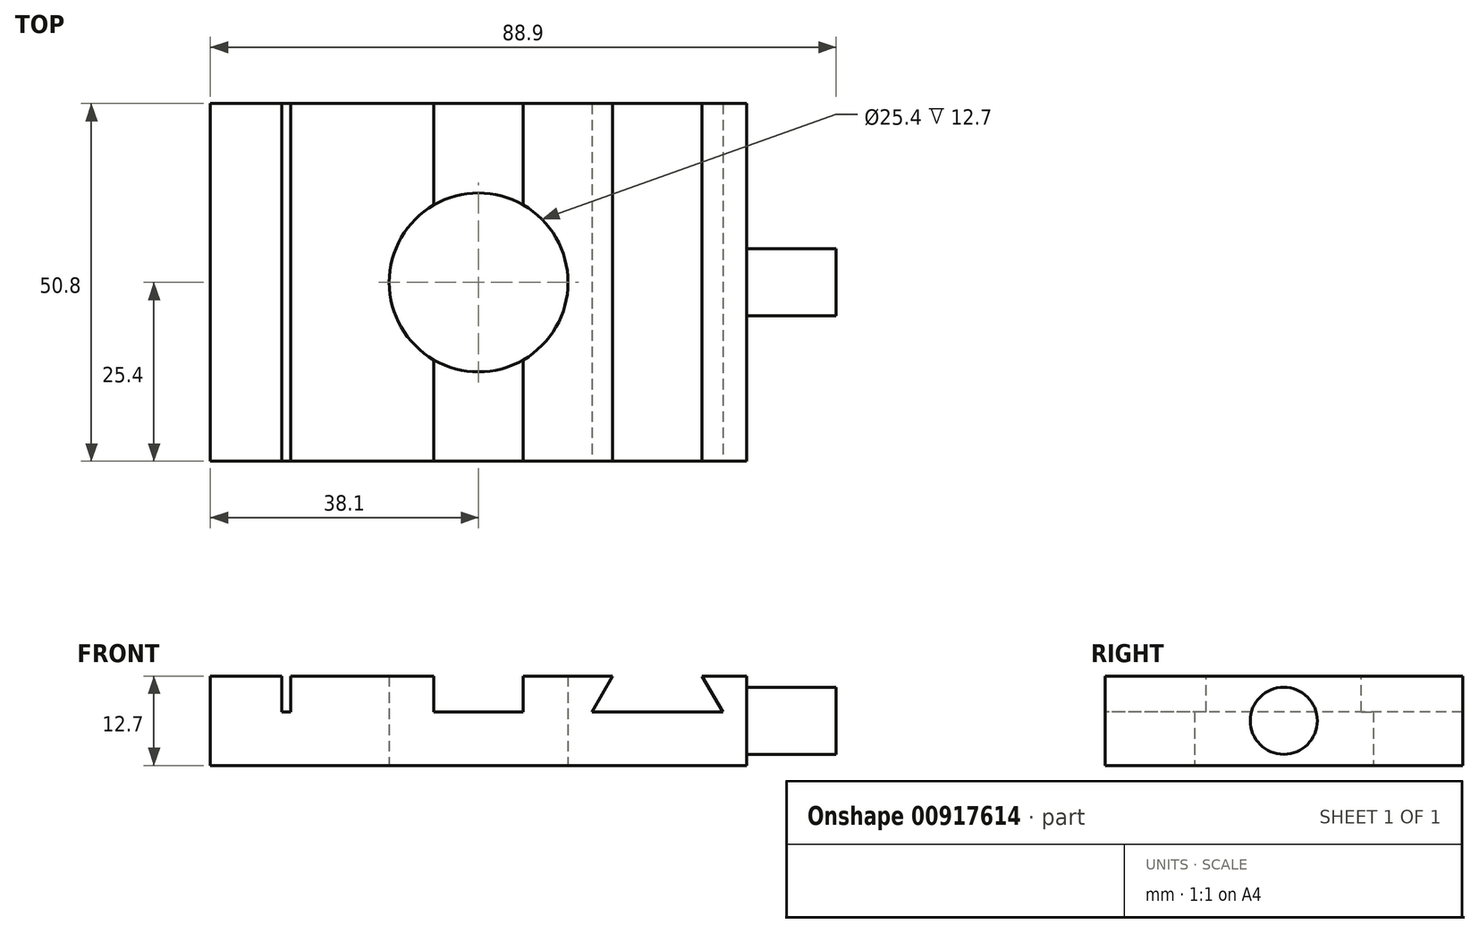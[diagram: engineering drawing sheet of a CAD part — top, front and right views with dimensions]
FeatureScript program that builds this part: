
annotation { "Feature Type Name" : "Feature", "Feature Type Description" : "" }
export const myFeature = defineFeature(function(context is Context, id is Id, definition is map)
    precondition{}
    {
        {
            var Q0;
            Q0=qCreatedBy(makeId("Top.planeOp"),FACE);
            var sketch = newSketch(context, id + "F0", { "sketchPlane" : qUnion([Q0])});
            skLineSegment(sketch, "E0.bottom", {"start": v(-38.1, 25.4) * mm, "end": v(38.1, 25.4) * mm});
            skLineSegment(sketch, "E0.top", {"start": v(-38.1, -25.4) * mm, "end": v(38.1, -25.4) * mm});
            skLineSegment(sketch, "E0.left", {"start": v(-38.1, 25.4) * mm, "end": v(-38.1, -25.4) * mm});
            skLineSegment(sketch, "E0.right", {"start": v(38.1, 25.4) * mm, "end": v(38.1, -25.4) * mm});
            skPoint(sketch, "E0.middle", {"position": v(0, 0) * mm});
            skCircle(sketch, "E1", {"center": v(0, 0) * mm, "radius": 12.7 * mm});
            skSolve(sketch);
        }
        {
            var Q0;
            Q0=makeQuery(id+"F0.imprint","IMPRINT",FACE,{"disambiguationData":[TD([[makeQuery(id+"F0.imprint","IMPRINT",EDGE,{"derivedFrom":sQuery(id+"F0.wireOp",EDGE,"E0.bottom")}),-1.0]])]});
            extrude(context, id + "F1", {"entities" : qUnion([Q0]), "flatOperationType" : FlatOperationType.REMOVE, "depth" : 12.7 * mm, "offsetDistance" : 25.4 * mm, "domain" : OperationDomain.MODEL});
        }
        {
            var Q0;
            Q0=makeQuery(id+"F1.opExtrude","CAP_FACE",FACE,{"disambiguationData":[OSD([sQuery(id+"F0.wireOp",EDGE,"E0.bottom"),sQuery(id+"F0.wireOp",EDGE,"E0.top"),sQuery(id+"F0.wireOp",EDGE,"E0.left"),sQuery(id+"F0.wireOp",EDGE,"E0.right"),sQuery(id+"F0.wireOp",EDGE,"E1")])],"isStart":false});
            var sketch = newSketch(context, id + "F2", { "sketchPlane" : qUnion([Q0])});
            skLineSegment(sketch, "E2.bottom", {"start": v(-27.94, 25.4) * mm, "end": v(-26.67, 25.4) * mm});
            skLineSegment(sketch, "E2.top", {"start": v(-27.94, -25.4) * mm, "end": v(-26.67, -25.4) * mm});
            skLineSegment(sketch, "E2.left", {"start": v(-27.94, 25.4) * mm, "end": v(-27.94, -25.4) * mm});
            skLineSegment(sketch, "E2.right", {"start": v(-26.67, 25.4) * mm, "end": v(-26.67, -25.4) * mm});
            skPoint(sketch, "E3", {"position": v(0, 0) * mm});
            skLineSegment(sketch, "E4.bottom", {"start": v(-6.35, 25.4) * mm, "end": v(6.35, 25.4) * mm});
            skLineSegment(sketch, "E4.top", {"start": v(-6.35, -25.4) * mm, "end": v(6.35, -25.4) * mm});
            skLineSegment(sketch, "E4.left", {"start": v(-6.35, 25.4) * mm, "end": v(-6.35, -25.4) * mm});
            skLineSegment(sketch, "E4.right", {"start": v(6.35, 25.4) * mm, "end": v(6.35, -25.4) * mm});
            skLineSegment(sketch, "E5", {"start": v(0, 25.4) * mm, "end": v(0, -25.4) * mm, "construction": true});
            skSolve(sketch);
        }
        {
            var Q0;
            Q0=makeQuery(id+"F2.imprint","IMPRINT",FACE,{"disambiguationData":[TD([[makeQuery(id+"F2.imprint","IMPRINT",EDGE,{"derivedFrom":sQuery(id+"F2.wireOp",EDGE,"E2.bottom")}),-1.0]])]});
            var Q1;
            {var subQ0=sQuery(id+"F2.wireOp",EDGE,"E4.bottom");Q1=makeQuery(id+"F2.imprint","IMPRINT",FACE,{"disambiguationData":[TD([[makeQuery(id+"F2.imprint","IMPRINT",EDGE,{"derivedFrom":subQ0}),-1.0]])]});}
            var Q2;
            {var subQ0=sQuery(id+"F2.wireOp",EDGE,"E4.top");Q2=makeQuery(id+"F2.imprint","IMPRINT",FACE,{"disambiguationData":[TD([[makeQuery(id+"F2.imprint","IMPRINT",EDGE,{"derivedFrom":subQ0}),1.0]])]});}
            extrude(context, id + "F3", {"entities" : qUnion([Q0, Q1, Q2]), "operationType" : NewBodyOperationType.REMOVE, "oppositeDirection" : true, "depth" : 5.08 * mm, "offsetDistance" : 25.4 * mm});
        }
        {
            var Q0;
            Q0=makeQuery(id+"F1.opExtrude","SWEPT_FACE",FACE,{"disambiguationData":[OSD([sQuery(id+"F0.wireOp",EDGE,"E0.top")])]});
            var sketch = newSketch(context, id + "F4", { "sketchPlane" : qUnion([Q0])});
            skLineSegment(sketch, "E6", {"start": v(19.05, 12.7) * mm, "end": v(16.12, 7.62) * mm});
            skLineSegment(sketch, "E7", {"start": v(16.12, 7.62) * mm, "end": v(34.68, 7.62) * mm});
            skLineSegment(sketch, "E8", {"start": v(34.68, 7.62) * mm, "end": v(31.75, 12.7) * mm});
            skLineSegment(sketch, "E9", {"start": v(31.75, 12.7) * mm, "end": v(19.05, 12.7) * mm});
            skLineSegment(sketch, "E10", {"start": v(25.4, 7.62) * mm, "end": v(25.4, 12.7) * mm, "construction": true});
            skSolve(sketch);
        }
        {
            var Q0;
            Q0=makeQuery(id+"F4.imprint","IMPRINT",FACE,{"disambiguationData":[TD([[makeQuery(id+"F4.imprint","IMPRINT",EDGE,{"derivedFrom":sQuery(id+"F4.wireOp",EDGE,"E6")}),1.0]])]});
            extrude(context, id + "F5", {"entities" : qUnion([Q0]), "operationType" : NewBodyOperationType.REMOVE, "endBound" : BoundingType.THROUGH_ALL, "oppositeDirection" : true, "depth" : 25.4 * mm, "offsetDistance" : 25.4 * mm});
        }
        {
            var Q0;
            Q0=makeQuery(id+"F1.opExtrude","SWEPT_FACE",FACE,{"disambiguationData":[OSD([sQuery(id+"F0.wireOp",EDGE,"E0.right")])]});
            var sketch = newSketch(context, id + "F6", { "sketchPlane" : qUnion([Q0])});
            skCircle(sketch, "E11", {"center": v(0, 6.35) * mm, "radius": 4.76 * mm});
            skPoint(sketch, "E11.centerSnap0", {"position": v(0, 12.7) * mm});
            skPoint(sketch, "E11.centerSnap1", {"position": v(-25.4, 6.35) * mm});
            skSolve(sketch);
        }
        {
            var Q0;
            Q0=makeQuery(id+"F6.imprint","IMPRINT",FACE,{"disambiguationData":[TD([[makeQuery(id+"F6.imprint","IMPRINT",EDGE,{"derivedFrom":sQuery(id+"F6.wireOp",EDGE,"E11")}),1.0]])]});
            extrude(context, id + "F7", {"entities" : qUnion([Q0]), "operationType" : NewBodyOperationType.ADD, "depth" : 12.7 * mm, "offsetDistance" : 25.4 * mm});
        }
    });
